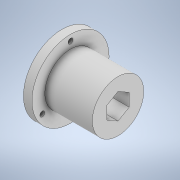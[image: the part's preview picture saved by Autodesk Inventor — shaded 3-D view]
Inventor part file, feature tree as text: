
AUTODESK INVENTOR PART (.ipt)
format: ipt  version: 2021 (Build 250183000, 183)  size: 137,728 bytes
history: native  units: mm
features: sketch x4, extrude x3
ambient origin geometry x8: Origin, YZ Plane, XZ Plane, XY Plane, X Axis, Y Axis, Z Axis, Center Point
bodies: Solid1 (feature_tree)
feature tree (7):
  extrude  "Extrusion1"  Depth=7.5mm
  extrude  "Extrusion2"  Depth=32.75mm
  extrude  "Extrusion3"  Depth=5.0mm TaperAngle=360.0deg
  sketch  "Sketch4"  dims[d13=5.0mm d14=0.0mm]
  sketch  "Sketch1"  dims[d0=30.0mm d1=7.5mm]
  sketch  "Sketch2"  dims[d2=32.75mm d3=0.0mm d4=45.0mm]
  sketch  "Sketch3"  dims[d5=5.0mm d6=0.0mm d9=30.0mm d11=360.0deg]
